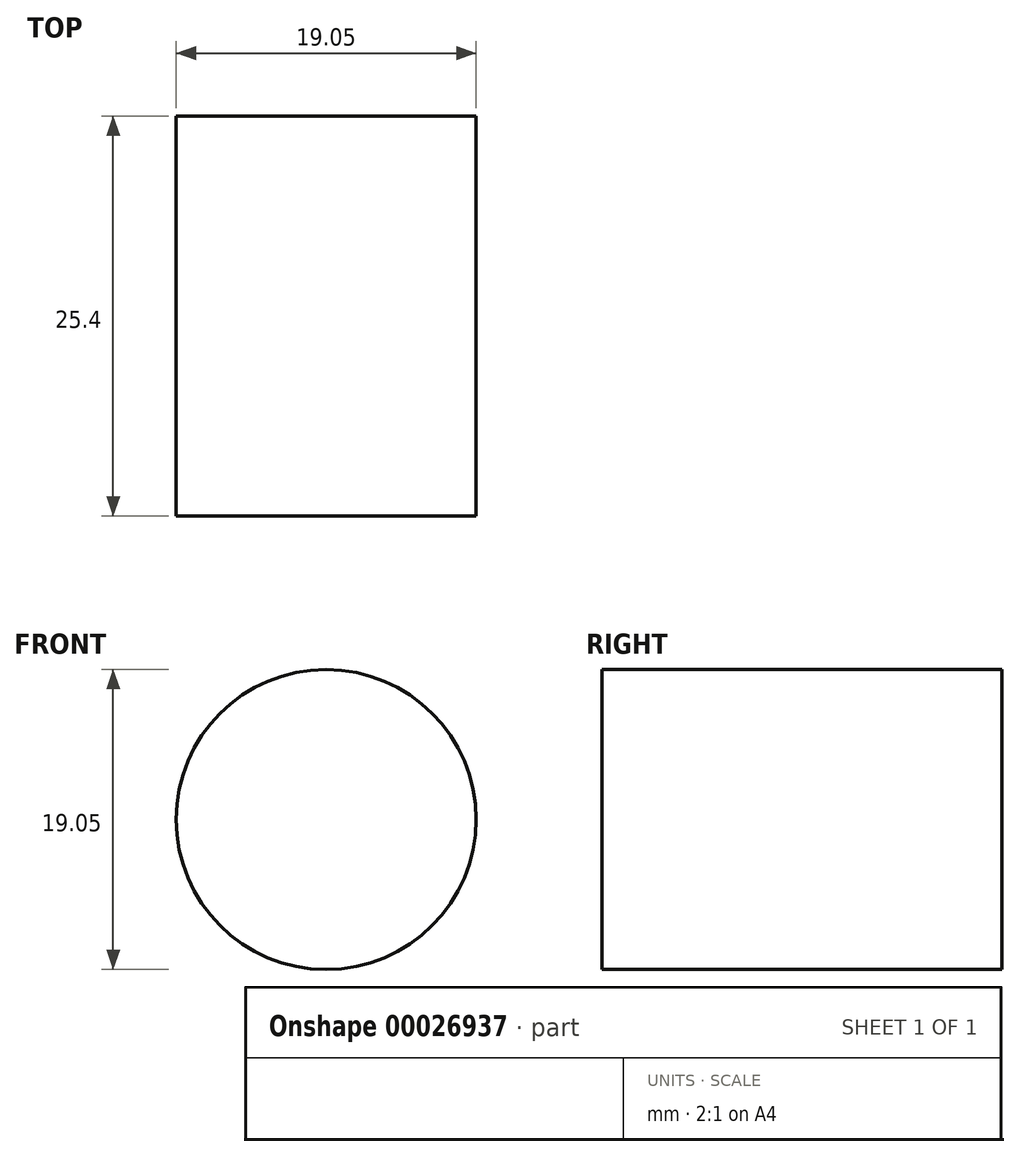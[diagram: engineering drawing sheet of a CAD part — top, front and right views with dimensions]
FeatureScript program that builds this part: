
annotation { "Feature Type Name" : "Feature", "Feature Type Description" : "" }
export const myFeature = defineFeature(function(context is Context, id is Id, definition is map)
    precondition{}
    {
        {
            var Q0;
            Q0=qCreatedBy(makeId("Front.planeOp"),FACE);
            var sketch = newSketch(context, id + "F0", { "sketchPlane" : qUnion([Q0])});
            skCircle(sketch, "E0", {"center": v(-13.42, 7.36) * mm, "radius": 9.52 * mm});
            skSolve(sketch);
        }
        {
            var Q0;
            Q0=makeQuery(id+"F0.imprint","IMPRINT",FACE,{"disambiguationData":[TD([[makeQuery(id+"F0.imprint","IMPRINT",EDGE,{"derivedFrom":sQuery(id+"F0.wireOp",EDGE,"E0")}),1.0]])]});
            extrude(context, id + "F1", {"entities" : qUnion([Q0]), "depth" : 25.4 * mm});
        }
    });
